# Revit family: IS_Connect_Multiproduct_BIM_DE;e7970;e7971
name_source: partatom
category: Plumbing Fixtures
revit_build: Autodesk Revit MEP 2014 (Build: 20130308_1515(x64)
units: mm (PartAtom-declared; Revit-internal decimal feet)

## types (4) — shared parameters
Accessories = www.idealstandard.de\ersatzteile
AreaUnits = millimeters
Assembly Code = C1030200
AssetType = Fixed
Brand = Ideal Standard
CodePerformance = DIN EN 997, CL1-6-VRII, DIN EN 33
ConnectionType = Plumbing
DurationUnit = year
ExpectedLife = 25
GrossWeight = 0
IfcExportAs = IfcSanitaryTerminalType
IfcExportType = CISTERN
InstallationInstructions = www.idealstandard.de\produkte
LinearUnits = millimeters
ManufacturerURL = www.idealstandard.com
NBSDescription = WC cistern fittings
NBSReference = 45-30-70/387
NominalDepth = 177 mm  [stored 0.580709 ft]
NominalHeight = 376 mm
NominalLength = 177 mm  [stored 0.580709 ft]
NominalWidth = 315 mm
ProductInformation = www.idealstandard.de/produkte
Shape = Sculptured
Size = 313x176x376mm
Space = Internal
ToiletPanType = WashDown
ToiletType = Other
URL = www.idealstandard.com
Uniclass2015Code = Pr_40_20_93_89
Uniclass2015Title = WC cisterns
Uniclass2015Version = Products v1.1
Version = 1
VolumeUnits = Litres
WarrantyDescription = Manufacturers Warranty
WarrantyDurationUnit = year
zero-valued in all types: CWFU, Cost, Default Elevation, HWFU, SpilloverLevel, WFU

## per-type parameters (varying)
| type | BIMObjectName | BarCode | Description | E7970 - bottom inlet | E7971-Side inlet | Features | Finish | Model | ModelNumber | ModelReference | Name | NettWeight |
| E797001 - Connect Cube 6 litre cistern, inlet below | ISI_IdealStandard_WcCisterns_ConnectCube_E797001 | 5017830390435 | E797001 Connect Cube 6 litre cistern, inlet below | Yes | No | Connect Cube 6 litre cistern, inlet below | white | E797001 | E797001 | Connect Cube 6 litre cistern, inlet below | WcCisterns_ConnectCube_E797001_IdealStandard | 13,51 kg |
| E7970MA - Connect Cube 6 litre cistern, inlet below | ISI_IdealStandard_WcCisterns_ConnectCube_E7970MA | 5017830395805 | E7970MA Connect Cube 6 litre cistern, inlet below | Yes | No | Connect Cube 6 litre cistern, inlet below | white with ideal plus | E7970MA | E7970MA | Connect Cube 6 litre cistern, inlet below | WcCisterns_ConnectCube_E7970MA_IdealStandard | 13,61 kg |
| E797101 - Connect Cube 6 litre cistern, inlet lateral | ISI_IdealStandard_WcCisterns_ConnectCube_E797101 | 5017830390442 | E797101 Connect Cube 6 litre cistern, inlet lateral | No | Yes | Connect Cube 6 litre cistern, inlet lateral | white | E797101 | E797101 | Connect Cube 6 litre cistern, inlet lateral | WcCisterns_ConnectCube_E797101_IdealStandard | 13,49 kg |
| E7971MA - Connect Cube 6 litre cistern, inlet lateral | ISI_IdealStandard_WcCisterns_ConnectCube_E7971MA | 5017830398950 | E7971MA Connect Cube 6 litre cistern, inlet lateral | No | Yes | Connect Cube 6 litre cistern, inlet lateral | white with ideal plus | E7971MA | E7971MA | Connect Cube 6 litre cistern, inlet lateral | WcCisterns_ConnectCube_E7971MA_IdealStandard | 13,58 kg |

note: [stored X ft] marks values corroborated as IEEE doubles in the binary element streams (Revit-internal decimal feet)

## geometry (parser evidence)
native form markers: Blend x2, Sweep x1
no freeform markers — native parametric forms only
